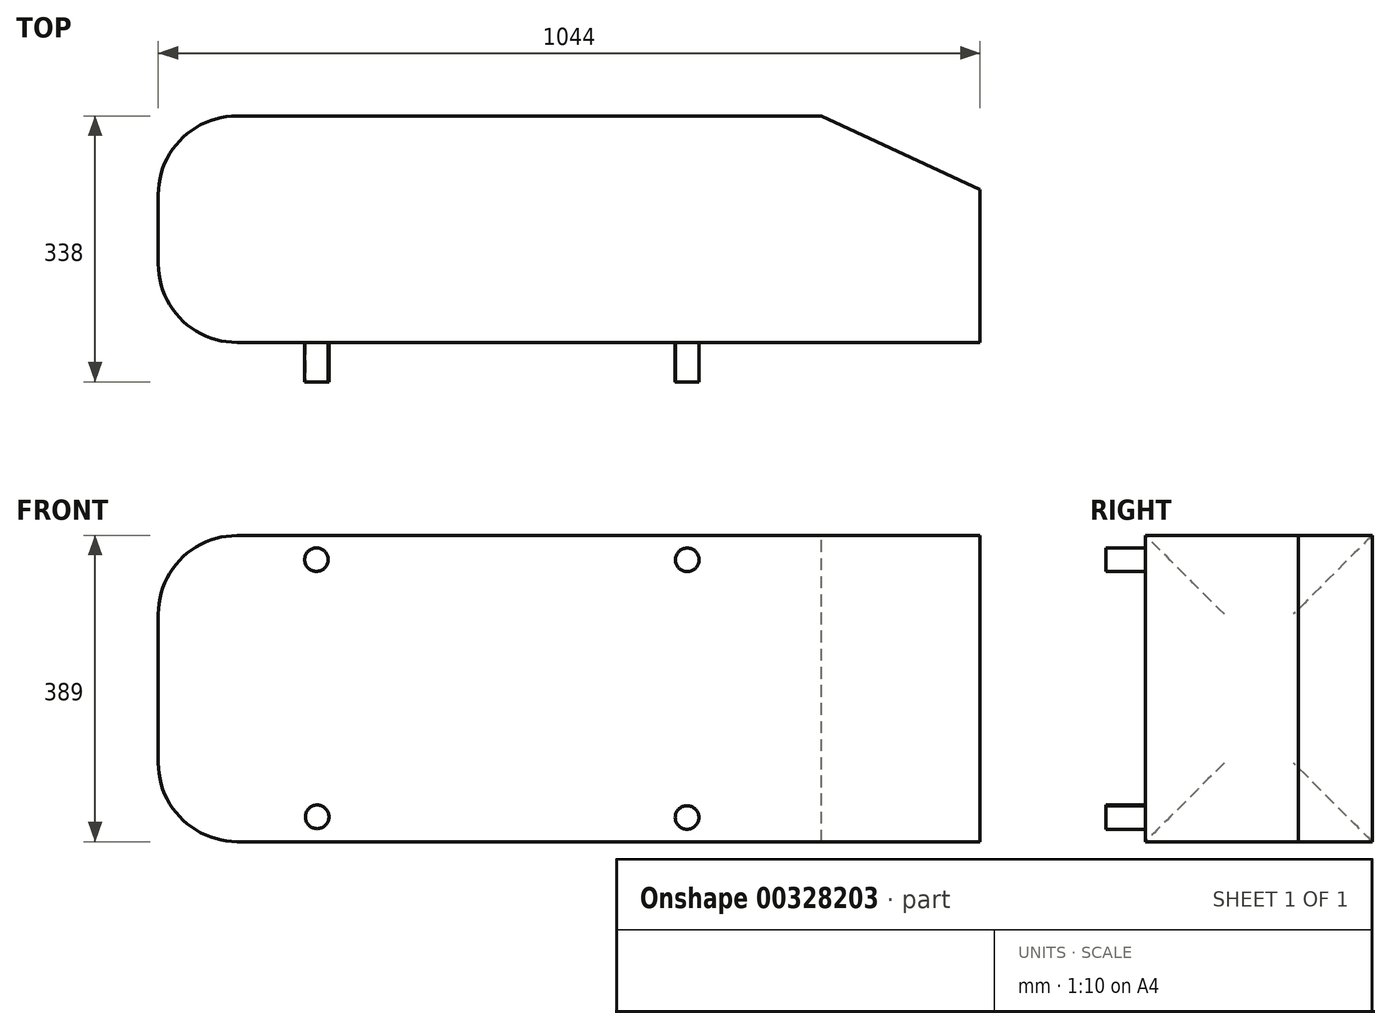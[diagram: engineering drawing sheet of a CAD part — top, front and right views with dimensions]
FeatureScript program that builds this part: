
annotation { "Feature Type Name" : "Feature", "Feature Type Description" : "" }
export const myFeature = defineFeature(function(context is Context, id is Id, definition is map)
    precondition{}
    {
        {
            var Q0;
            Q0=qCreatedBy(makeId("Top.planeOp"),FACE);
            var sketch = newSketch(context, id + "F0", { "sketchPlane" : qUnion([Q0])});
            skLineSegment(sketch, "E0", {"start": v(-1044, 0) * mm, "end": v(0, 0) * mm});
            skLineSegment(sketch, "E1", {"start": v(0, 0) * mm, "end": v(0, 194.18) * mm});
            skLineSegment(sketch, "E2", {"start": v(0, 194.18) * mm, "end": v(-201.2, 288) * mm});
            skLineSegment(sketch, "E3", {"start": v(-201.2, 288) * mm, "end": v(-1044, 288) * mm});
            skLineSegment(sketch, "E4", {"start": v(-1044, 288) * mm, "end": v(-1044, 0) * mm});
            skSolve(sketch);
        }
        {
            var Q0;
            Q0=makeQuery(id+"F0.imprint","IMPRINT",FACE,{"disambiguationData":[TD([[makeQuery(id+"F0.imprint","IMPRINT",EDGE,{"derivedFrom":sQuery(id+"F0.wireOp",EDGE,"E0")}),1.0]])]});
            extrude(context, id + "F1", {"entities" : qUnion([Q0]), "oppositeDirection" : true, "depth" : 389 * mm});
        }
        {
            var Q0;
            Q0=makeQuery(id+"F1.opExtrude","SWEPT_FACE",FACE,{"disambiguationData":[OSD([sQuery(id+"F0.wireOp",EDGE,"E4")])]});
            fillet(context, id + "F2", {"entities" : qUnion([Q0]), "radius" : 100 * mm, "tangentPropagation" : true, "allowEdgeOverflow" : false});
        }
        {
            var Q0;
            Q0=qCreatedBy(makeId("Front.planeOp"),FACE);
            cPlane(context, id + "F3", {"entities" : qUnion([Q0]), "cplaneType" : CPlaneType.OFFSET, "offset" : 50 * mm, "width" : 150 * mm, "height" : 150 * mm});
        }
        {
            var Q0;
            Q0=qCreatedBy(id+"F3.planeOp",FACE);
            var sketch = newSketch(context, id + "F4", { "sketchPlane" : qUnion([Q0])});
            skLineSegment(sketch, "E5", {"start": v(-895.23, -31) * mm, "end": v(-14.3, -31) * mm, "construction": true});
            skLineSegment(sketch, "E6", {"start": v(-876.7, -358) * mm, "end": v(-73.6, -358) * mm, "construction": true});
            skLineSegment(sketch, "E7", {"start": v(-843, 144.38) * mm, "end": v(-843, -480.84) * mm, "construction": true});
            skLineSegment(sketch, "E8", {"start": v(-372, 160.36) * mm, "end": v(-372, -495.83) * mm, "construction": true});
            skCircle(sketch, "E9", {"center": v(-372, -31) * mm, "radius": 15 * mm});
            skSolve(sketch);
        }
        {
            var Q0;
            Q0=qCreatedBy(id+"F3.planeOp",FACE);
            var sketch = newSketch(context, id + "F5", { "sketchPlane" : qUnion([Q0])});
            skCircle(sketch, "E10", {"center": v(-372.28, -358.3) * mm, "radius": 15 * mm});
            skSolve(sketch);
        }
        {
            var Q0;
            Q0=qCreatedBy(id+"F3.planeOp",FACE);
            var sketch = newSketch(context, id + "F6", { "sketchPlane" : qUnion([Q0])});
            skCircle(sketch, "E11", {"center": v(-843.02, -30.76) * mm, "radius": 15 * mm});
            skSolve(sketch);
        }
        {
            var Q0;
            Q0=qCreatedBy(id+"F3.planeOp",FACE);
            var sketch = newSketch(context, id + "F7", { "sketchPlane" : qUnion([Q0])});
            skCircle(sketch, "E12", {"center": v(-842.1, -357.53) * mm, "radius": 15 * mm});
            skSolve(sketch);
        }
        {
            var Q0;
            Q0=makeQuery(id+"F7.imprint","IMPRINT",FACE,{"disambiguationData":[TD([[makeQuery(id+"F7.imprint","IMPRINT",EDGE,{"derivedFrom":sQuery(id+"F7.wireOp",EDGE,"E12")}),1.0]])]});
            extrude(context, id + "F8", {"entities" : qUnion([Q0]), "operationType" : NewBodyOperationType.ADD, "oppositeDirection" : true, "depth" : 50 * mm});
        }
        {
            var Q0;
            Q0=makeQuery(id+"F5.imprint","IMPRINT",FACE,{"disambiguationData":[TD([[makeQuery(id+"F5.imprint","IMPRINT",EDGE,{"derivedFrom":sQuery(id+"F5.wireOp",EDGE,"E10")}),1.0]])]});
            var Q1;
            Q1=makeQuery(id+"F4.imprint","IMPRINT",FACE,{"disambiguationData":[TD([[makeQuery(id+"F4.imprint","IMPRINT",EDGE,{"derivedFrom":sQuery(id+"F4.wireOp",EDGE,"E9")}),1.0]])]});
            var Q2;
            Q2=makeQuery(id+"F6.imprint","IMPRINT",FACE,{"disambiguationData":[TD([[makeQuery(id+"F6.imprint","IMPRINT",EDGE,{"derivedFrom":sQuery(id+"F6.wireOp",EDGE,"E11")}),1.0]])]});
            extrude(context, id + "F9", {"entities" : qUnion([Q0, Q1, Q2]), "operationType" : NewBodyOperationType.ADD, "oppositeDirection" : true, "depth" : 50 * mm});
        }
    });
